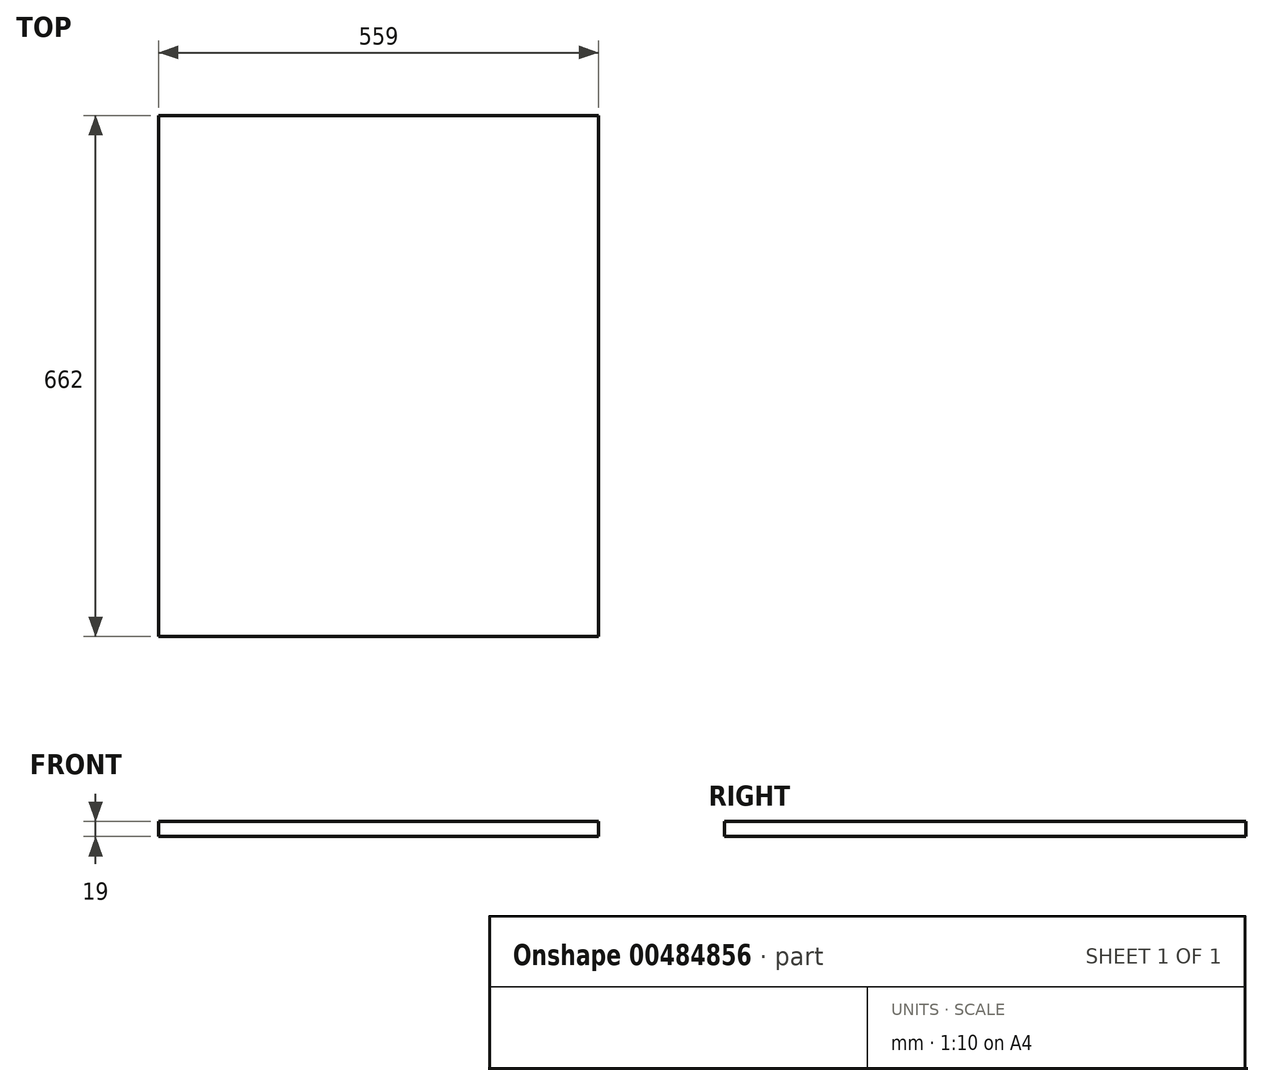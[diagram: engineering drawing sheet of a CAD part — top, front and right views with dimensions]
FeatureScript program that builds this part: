
annotation { "Feature Type Name" : "Feature", "Feature Type Description" : "" }
export const myFeature = defineFeature(function(context is Context, id is Id, definition is map)
    precondition{}
    {
        {
            var Q0;
            Q0=qCreatedBy(makeId("Top.planeOp"),FACE);
            var sketch = newSketch(context, id + "F0", { "sketchPlane" : qUnion([Q0])});
            skLineSegment(sketch, "E0.bottom", {"start": v(-121.2, 601.8) * mm, "end": v(437.8, 601.8) * mm});
            skLineSegment(sketch, "E0.top", {"start": v(-121.2, -60.2) * mm, "end": v(437.8, -60.2) * mm});
            skLineSegment(sketch, "E0.left", {"start": v(-121.2, 601.8) * mm, "end": v(-121.2, -60.2) * mm});
            skLineSegment(sketch, "E0.right", {"start": v(437.8, 601.8) * mm, "end": v(437.8, -60.2) * mm});
            skSolve(sketch);
        }
        {
            var Q0;
            Q0 = qSketchRegion(id + "F0", true);
            extrude(context, id + "F1", {"entities" : qUnion([Q0]), "depth" : 19 * mm});
        }
    });
